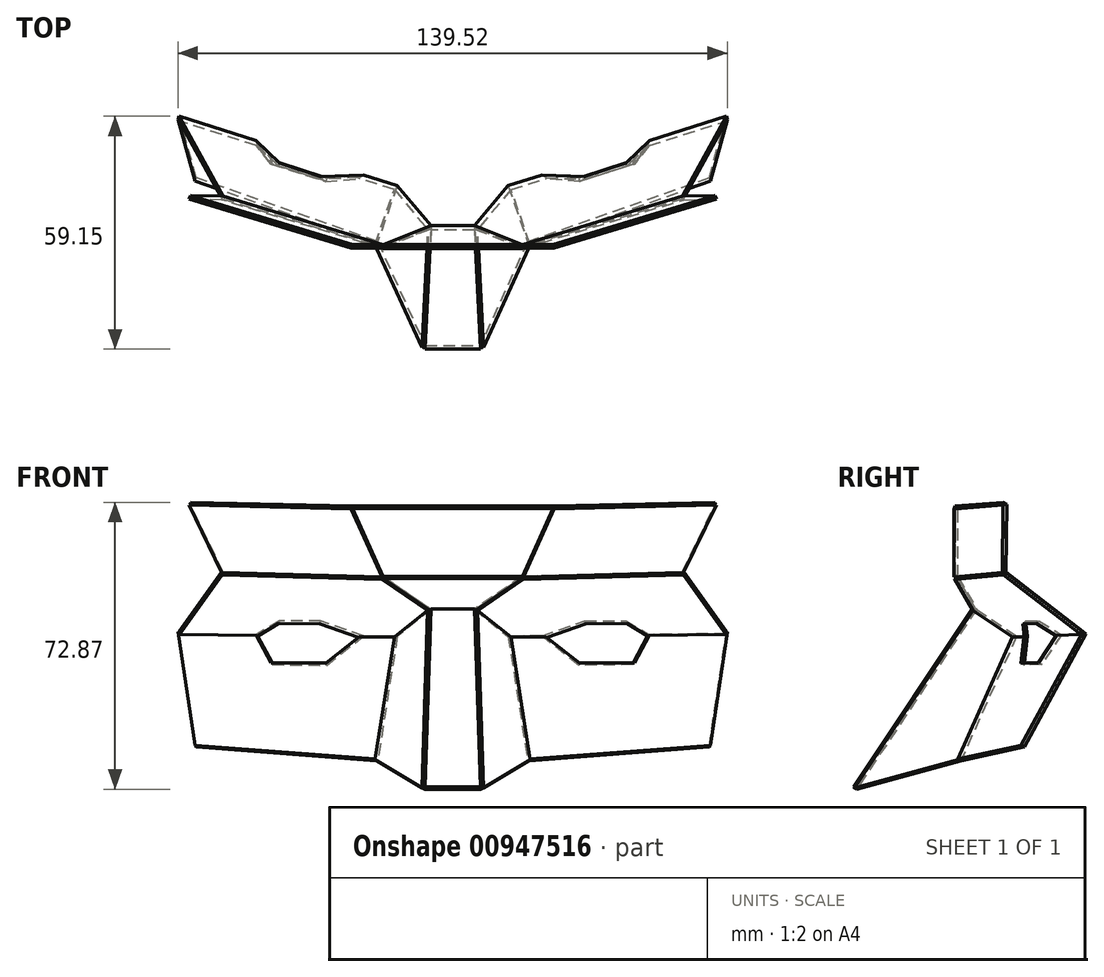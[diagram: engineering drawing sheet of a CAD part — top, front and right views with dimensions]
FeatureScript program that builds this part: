
annotation { "Feature Type Name" : "Feature", "Feature Type Description" : "" }
export const myFeature = defineFeature(function(context is Context, id is Id, definition is map)
    precondition{}
    {
        {
            assignVariable(context, id + "F0", {"variableType" : VariableType.LENGTH, "name" : "Thickness", "lengthValue" : 1 * mm});
        }
        {
            var Q0;
            Q0=qCreatedBy(makeId("Top.planeOp"),FACE);
            var sketch = newSketch(context, id + "F1", { "sketchPlane" : qUnion([Q0])});
            skLineSegment(sketch, "E0", {"start": v(0, -40) * mm, "end": v(7.5, -40) * mm});
            skLineSegment(sketch, "E1", {"start": v(7.5, -40) * mm, "end": v(22.5, 0) * mm});
            skSolve(sketch);
        }
        {
            var Q0;
            Q0=qCreatedBy(makeId("Right.planeOp"),FACE);
            var sketch = newSketch(context, id + "F2", { "sketchPlane" : qUnion([Q0])});
            skLineSegment(sketch, "E2", {"start": v(-40, 0) * mm, "end": v(0, 60) * mm});
            skSolve(sketch);
        }
        {
            var Q0;
            Q0=sQuery(id+"F2.wireOp",EDGE,"E2");
            var Q1;
            Q1=sQuery(id+"F1.wireOp",EDGE,"E0");
            cPlane(context, id + "F3", {"entities" : qUnion([Q0, Q1]), "cplaneType" : CPlaneType.LINE_ANGLE, "offset" : 25 * mm, "angle" : 0 * degree, "width" : 150 * mm, "height" : 150 * mm});
        }
        {
            var Q0;
            Q0=qCreatedBy(id+"F3.planeOp",FACE);
            var sketch = newSketch(context, id + "F4", { "sketchPlane" : qUnion([Q0])});
            skLineSegment(sketch, "E3.bottom", {"start": v(0, 49.92) * mm, "end": v(-5.5, 49.92) * mm});
            skLineSegment(sketch, "E3.top", {"start": v(0, -5.08) * mm, "end": v(-7, -5.08) * mm});
            skLineSegment(sketch, "E3.left", {"start": v(0, 49.92) * mm, "end": v(0, -5.08) * mm});
            skLineSegment(sketch, "E3.right", {"start": v(-5.5, 49.92) * mm, "end": v(-7, -5.08) * mm});
            skSolve(sketch);
        }
        {
            var Q0;
            Q0=sQuery(id+"F4.wireOp",EDGE,"E3.right");
            var Q1;
            Q1=qCreatedBy(id+"F3.planeOp",FACE);
            cPlane(context, id + "F5", {"entities" : qUnion([Q0, Q1]), "cplaneType" : CPlaneType.LINE_ANGLE, "offset" : 25 * mm, "angle" : 55 * degree, "oppositeDirection" : true, "width" : 150 * mm, "height" : 150 * mm});
        }
        {
            var Q0;
            Q0=qCreatedBy(id+"F5.planeOp",FACE);
            var sketch = newSketch(context, id + "F6", { "sketchPlane" : qUnion([Q0])});
            skLineSegment(sketch, "E4", {"start": v(-21.49, 10.5) * mm, "end": v(12.97, 53.4) * mm});
            skLineSegment(sketch, "E5", {"start": v(12.97, 53.4) * mm, "end": v(24.46, 43.75) * mm});
            skLineSegment(sketch, "E6", {"start": v(24.46, 43.75) * mm, "end": v(8.44, 12.63) * mm});
            skLineSegment(sketch, "E7", {"start": v(8.44, 12.63) * mm, "end": v(-21.49, 10.5) * mm});
            skSolve(sketch);
        }
        {
            var Q0;
            Q0=sQuery(id+"F6.wireOp",EDGE,"E6");
            var Q1;
            Q1=qCreatedBy(id+"F5.planeOp",FACE);
            cPlane(context, id + "F7", {"entities" : qUnion([Q0, Q1]), "cplaneType" : CPlaneType.LINE_ANGLE, "offset" : 25 * mm, "angle" : 40 * degree, "width" : 150 * mm, "height" : 150 * mm});
        }
        {
            var Q0;
            Q0=qCreatedBy(id+"F7.planeOp",FACE);
            var sketch = newSketch(context, id + "F8", { "sketchPlane" : qUnion([Q0])});
            skLineSegment(sketch, "E8", {"start": v(-9.66, 52.07) * mm, "end": v(-14.8, 17.45) * mm});
            skLineSegment(sketch, "E9", {"start": v(-14.8, 17.45) * mm, "end": v(-62.7, 27.81) * mm});
            skLineSegment(sketch, "E10", {"start": v(-62.7, 27.81) * mm, "end": v(-67.17, 60.5) * mm});
            skLineSegment(sketch, "E11", {"start": v(-67.17, 60.5) * mm, "end": v(-46.89, 57.53) * mm});
            skLineSegment(sketch, "E12", {"start": v(-46.89, 57.53) * mm, "end": v(-42.63, 48.48) * mm});
            skLineSegment(sketch, "E13", {"start": v(-42.63, 48.48) * mm, "end": v(-28.3, 46.35) * mm});
            skLineSegment(sketch, "E14", {"start": v(-28.3, 46.35) * mm, "end": v(-18.56, 53.38) * mm});
            skLineSegment(sketch, "E15", {"start": v(-18.56, 53.38) * mm, "end": v(-9.66, 52.07) * mm});
            skLineSegment(sketch, "E16", {"start": v(-46.89, 57.53) * mm, "end": v(-18.56, 53.38) * mm, "construction": true});
            skSolve(sketch);
        }
        {
            var Q0;
            Q0=sQuery(id+"F6.wireOp",VERTEX,"E5.end");
            var Q1;
            Q1=sQuery(id+"F8.wireOp",VERTEX,"E14.end");
            var Q2;
            Q2=sQuery(id+"F4.wireOp",VERTEX,"E3.bottom.end");
            cPlane(context, id + "F9", {"entities" : qUnion([Q0, Q1, Q2]), "cplaneType" : CPlaneType.THREE_POINT, "offset" : 25 * mm, "width" : 150 * mm, "height" : 150 * mm});
        }
        {
            var Q0;
            Q0=qCreatedBy(id+"F9.planeOp",FACE);
            var sketch = newSketch(context, id + "F10", { "sketchPlane" : qUnion([Q0])});
            skLineSegment(sketch, "E17", {"start": v(23.85, -29.02) * mm, "end": v(32.65, -27.1) * mm});
            skLineSegment(sketch, "E18", {"start": v(32.65, -27.1) * mm, "end": v(43.77, -30) * mm});
            skLineSegment(sketch, "E19", {"start": v(43.77, -30) * mm, "end": v(54.51, -27.6) * mm});
            skLineSegment(sketch, "E20", {"start": v(54.51, -27.6) * mm, "end": v(60.61, -20.99) * mm});
            skLineSegment(sketch, "E21", {"start": v(60.61, -20.99) * mm, "end": v(80.64, -16.62) * mm});
            skLineSegment(sketch, "E22", {"start": v(80.64, -16.62) * mm, "end": v(69.25, -42.2) * mm});
            skLineSegment(sketch, "E23", {"start": v(69.25, -42.2) * mm, "end": v(27.53, -50.3) * mm});
            skLineSegment(sketch, "E24", {"start": v(27.53, -50.3) * mm, "end": v(15.03, -41.14) * mm});
            skLineSegment(sketch, "E25", {"start": v(15.03, -41.14) * mm, "end": v(23.85, -29.02) * mm});
            skSolve(sketch);
        }
        {
            var Q0;
            Q0=sQuery(id+"F2.wireOp",VERTEX,"E2.end");
            var Q1;
            Q1=sQuery(id+"F4.wireOp",VERTEX,"E3.bottom.end");
            var Q2;
            Q2=sQuery(id+"F10.wireOp",VERTEX,"E23.end");
            cPlane(context, id + "F11", {"entities" : qUnion([Q0, Q1, Q2]), "cplaneType" : CPlaneType.THREE_POINT, "offset" : 25 * mm, "width" : 150 * mm, "height" : 150 * mm});
        }
        {
            var Q0;
            Q0=qCreatedBy(id+"F11.planeOp",FACE);
            var sketch = newSketch(context, id + "F12", { "sketchPlane" : qUnion([Q0])});
            skLineSegment(sketch, "E26", {"start": v(0, 52.02) * mm, "end": v(-5.5, 52.02) * mm});
            skLineSegment(sketch, "E27", {"start": v(-5.5, 52.02) * mm, "end": v(-17.7, 61.58) * mm});
            skLineSegment(sketch, "E28", {"start": v(-17.7, 61.58) * mm, "end": v(0, 61.58) * mm});
            skLineSegment(sketch, "E29", {"start": v(0, 61.58) * mm, "end": v(0, 52.02) * mm});
            skSolve(sketch);
        }
        {
            var Q0;
            Q0=qCreatedBy(id+"F11.planeOp",FACE);
            var Q1;
            Q1=sQuery(id+"F12.wireOp",EDGE,"E28");
            cPlane(context, id + "F13", {"entities" : qUnion([Q0, Q1]), "cplaneType" : CPlaneType.LINE_ANGLE, "offset" : 25 * mm, "angle" : 30 * degree, "width" : 150 * mm, "height" : 150 * mm});
        }
        {
            var Q0;
            Q0=qCreatedBy(id+"F13.planeOp",FACE);
            var sketch = newSketch(context, id + "F14", { "sketchPlane" : qUnion([Q0])});
            skLineSegment(sketch, "E30", {"start": v(0, 68.29) * mm, "end": v(17.7, 68.29) * mm});
            skLineSegment(sketch, "E31", {"start": v(17.7, 68.29) * mm, "end": v(25.5, 85.6) * mm});
            skLineSegment(sketch, "E32", {"start": v(25.5, 85.6) * mm, "end": v(0, 85.6) * mm});
            skLineSegment(sketch, "E33", {"start": v(0, 85.6) * mm, "end": v(0, 68.29) * mm});
            skSolve(sketch);
        }
        {
            var Q0;
            Q0=sQuery(id+"F14.wireOp",VERTEX,"E31.end");
            var Q1;
            Q1=sQuery(id+"F10.wireOp",VERTEX,"E23.end");
            var Q2;
            Q2=sQuery(id+"F10.wireOp",VERTEX,"E22.end");
            cPlane(context, id + "F15", {"entities" : qUnion([Q0, Q1, Q2]), "cplaneType" : CPlaneType.THREE_POINT, "offset" : 25 * mm, "width" : 150 * mm, "height" : 150 * mm});
        }
        {
            var Q0;
            Q0=qCreatedBy(id+"F15.planeOp",FACE);
            var sketch = newSketch(context, id + "F16", { "sketchPlane" : qUnion([Q0])});
            skLineSegment(sketch, "E34", {"start": v(-18.22, 68.32) * mm, "end": v(-60.72, 67.82) * mm});
            skLineSegment(sketch, "E35", {"start": v(-60.72, 67.82) * mm, "end": v(-69.37, 84.74) * mm});
            skLineSegment(sketch, "E36", {"start": v(-69.37, 84.74) * mm, "end": v(-26.38, 85.48) * mm});
            skLineSegment(sketch, "E37", {"start": v(-26.38, 85.48) * mm, "end": v(-18.22, 68.32) * mm});
            skSolve(sketch);
        }
        {
            var Q0;
            Q0 = qSketchRegion(id + "F4", true);
            extrude(context, id + "F17", {"entities" : qUnion([Q0]), "oppositeDirection" : true, "depth" : getVariable(context, 'Thickness'), "offsetDistance" : 25 * mm});
        }
        {
            var Q0;
            Q0 = qSketchRegion(id + "F6", true);
            extrude(context, id + "F18", {"entities" : qUnion([Q0]), "depth" : getVariable(context, 'Thickness'), "offsetDistance" : 25 * mm});
        }
        {
            var Q0;
            Q0 = qSketchRegion(id + "F8", true);
            extrude(context, id + "F19", {"entities" : qUnion([Q0]), "oppositeDirection" : true, "depth" : getVariable(context, 'Thickness'), "offsetDistance" : 25 * mm});
        }
        {
            var Q0;
            Q0 = qSketchRegion(id + "F10", true);
            extrude(context, id + "F20", {"entities" : qUnion([Q0]), "oppositeDirection" : true, "depth" : getVariable(context, 'Thickness'), "offsetDistance" : 25 * mm});
        }
        {
            var Q0;
            Q0 = qSketchRegion(id + "F12", true);
            extrude(context, id + "F21", {"entities" : qUnion([Q0]), "oppositeDirection" : true, "depth" : getVariable(context, 'Thickness'), "offsetDistance" : 25 * mm});
        }
        {
            var Q0;
            Q0 = qSketchRegion(id + "F14", true);
            extrude(context, id + "F22", {"entities" : qUnion([Q0]), "depth" : getVariable(context, 'Thickness'), "offsetDistance" : 25 * mm});
        }
        {
            var Q0;
            Q0 = qSketchRegion(id + "F16", true);
            extrude(context, id + "F23", {"entities" : qUnion([Q0]), "oppositeDirection" : true, "depth" : getVariable(context, 'Thickness'), "offsetDistance" : 25 * mm});
        }
        {
            var Q0;
            Q0 = qSketchRegion(id + "F4", true);
            var Q1;
            Q1 = qSketchRegion(id + "F6", true);
            var Q2;
            Q2 = qSketchRegion(id + "F8", true);
            var Q3;
            Q3 = qSketchRegion(id + "F10", true);
            var Q4;
            Q4 = qSketchRegion(id + "F12", true);
            var Q5;
            Q5 = qSketchRegion(id + "F14", true);
            var Q6;
            Q6 = qSketchRegion(id + "F16", true);
            extrude(context, id + "F24", {"entities" : qUnion([Q0, Q1, Q2, Q3, Q4, Q5, Q6]), "operationType" : NewBodyOperationType.ADD, "oppositeDirection" : true, "depth" : 1 * mm, "offsetDistance" : 25 * mm});
        }
        {
            var Q0;
            Q0=makeQuery(id+"F17.opExtrude","SWEPT_BODY",BODY,{"disambiguationData":[OSD([sQuery(id+"F4.wireOp",EDGE,"E3.bottom"),sQuery(id+"F4.wireOp",EDGE,"E3.top"),sQuery(id+"F4.wireOp",EDGE,"E3.left"),sQuery(id+"F4.wireOp",EDGE,"E3.right")])]});
            var Q1;
            Q1=qCreatedBy(makeId("Right.planeOp"),FACE);
            mirror(context, id + "F25", {"operationType" : NewBodyOperationType.ADD, "entities" : qUnion([Q0]), "mirrorPlane" : qUnion([Q1])});
        }
    });
